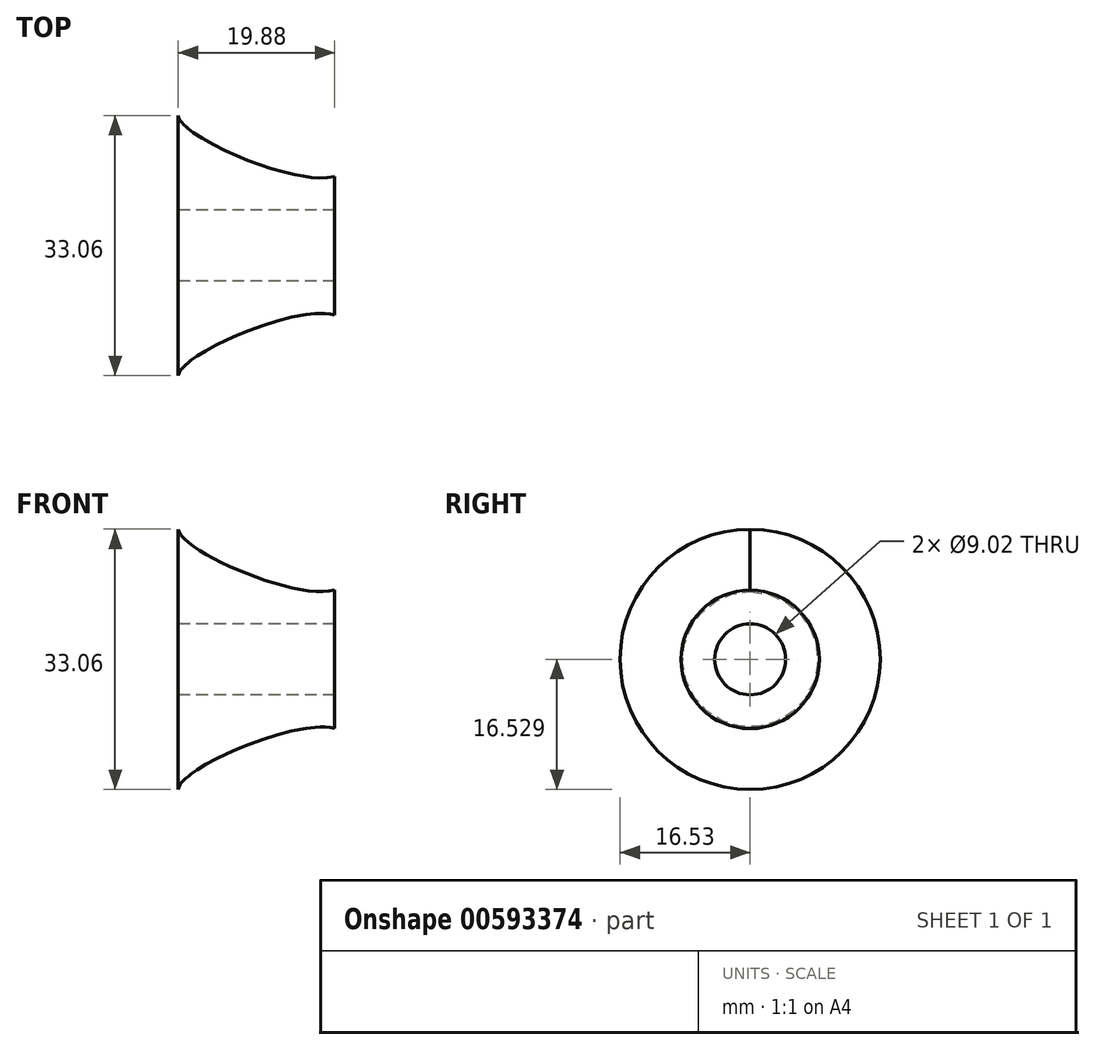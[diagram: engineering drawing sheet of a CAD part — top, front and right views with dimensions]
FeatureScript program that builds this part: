
annotation { "Feature Type Name" : "Feature", "Feature Type Description" : "" }
export const myFeature = defineFeature(function(context is Context, id is Id, definition is map)
    precondition{}
    {
        {
            var Q0;
            Q0=qCreatedBy(makeId("Front.planeOp"),FACE);
            var sketch = newSketch(context, id + "F0", { "sketchPlane" : qUnion([Q0])});
            skLineSegment(sketch, "E0", {"start": v(0, 0) * mm, "end": v(19.88, 0) * mm});
            skLineSegment(sketch, "E1", {"start": v(19.88, 0) * mm, "end": v(19.88, 4.28) * mm});
            skLineSegment(sketch, "E2", {"start": v(0, 0) * mm, "end": v(0, 12.02) * mm});
            skFitSpline(sketch, "E3", {"points": [v(0, 12.17) * mm, v(19.88, 4.28) * mm, v(19.88, 9.78) * mm, v(0, 12.17) * mm]});
            skLineSegment(sketch, "E4", {"start": v(0, -4.51) * mm, "end": v(19.66, -4.51) * mm});
            skSolve(sketch);
        }
        {
            var Q0;
            Q0=makeQuery(id+"F0.imprint","IMPRINT",FACE,{"disambiguationData":[TD([[makeQuery(id+"F0.imprint","IMPRINT",EDGE,{"derivedFrom":sQuery(id+"F0.wireOp",EDGE,"E0")}),1.0]])]});
            var Q1;
            Q1=sQuery(id+"F0.wireOp",EDGE,"E4");
            revolve(context, id + "F1", {"entities" : qUnion([Q0]), "axis" : qUnion([Q1]), "revolveType" : RevolveType.FULL});
        }
    });
